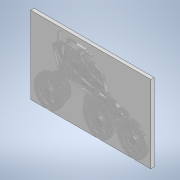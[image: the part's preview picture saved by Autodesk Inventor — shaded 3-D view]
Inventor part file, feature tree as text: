
AUTODESK INVENTOR PART (.ipt)
format: ipt  version: 2020.1 (Build 241239000, 239)  size: 2,403,840 bytes
history: native  units: mm
features: other x3, extrude x1, sketch x1
ambient origin geometry x8: Origin, YZ Plane, XZ Plane, XY Plane, X Axis, Y Axis, Z Axis, Center Point
bodies: Body1 (feature_tree)
feature tree (5):
  other  "Sólido1"
  other  "Rover 3 - Verde"
  extrude  "Extrusión1"  [1 undecoded]
  sketch  "Boceto1"  dims[d0=1.75mm d1=4.25mm d2=0.0mm d3=0.0mm]
  other  "MeshFeature1"
note: 1 required parameter value undecoded (feature->parameter linkage not recoverable at this tier; creation-order binding heuristic only, values carry confidence <= 0.55)
